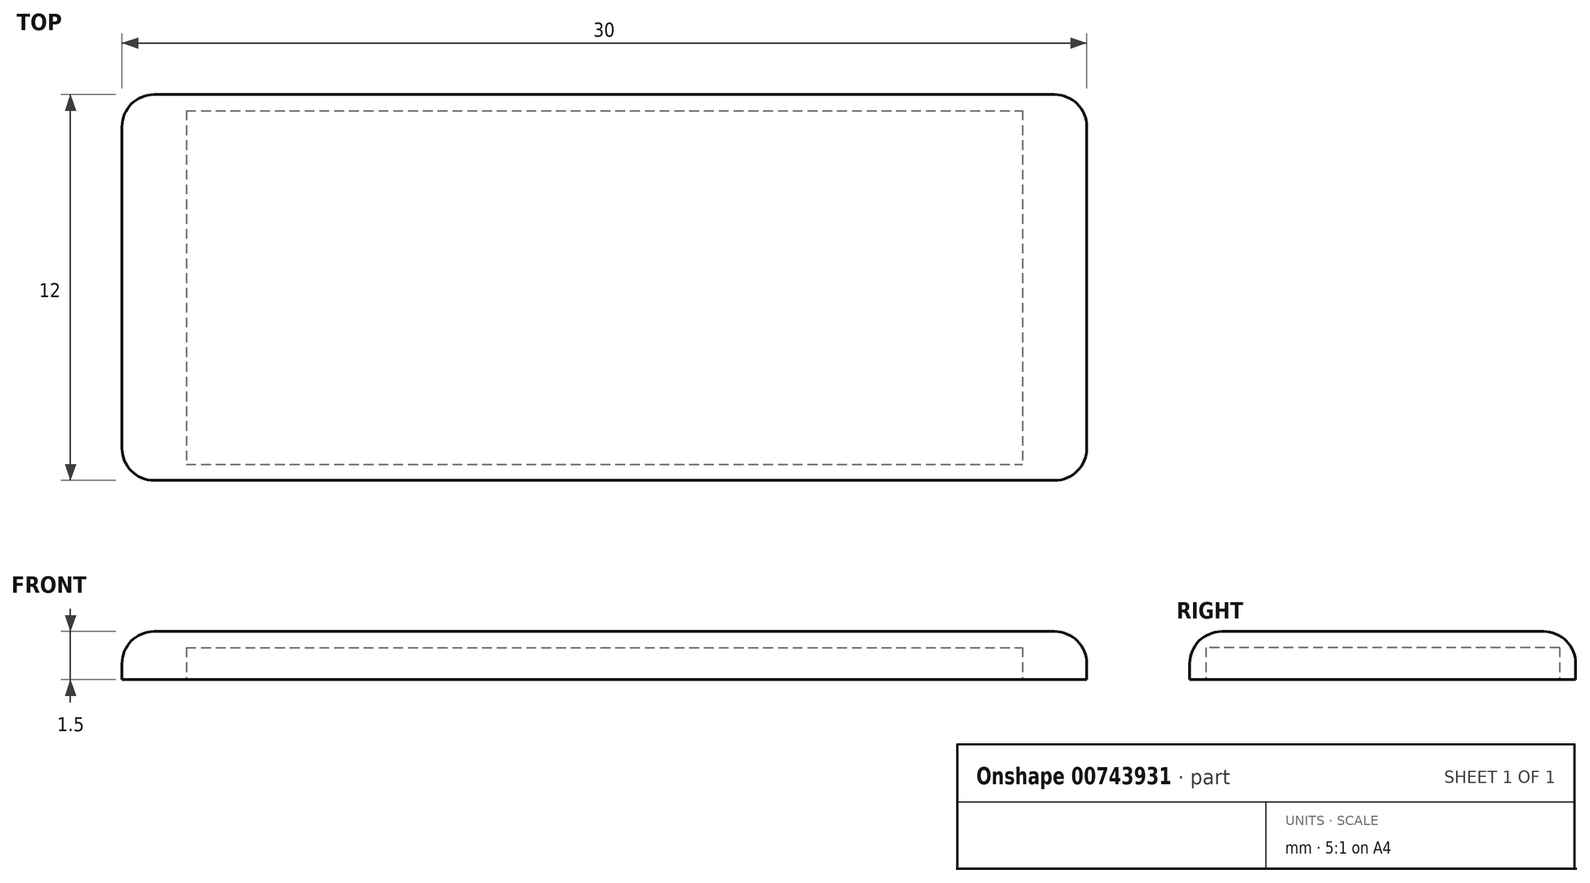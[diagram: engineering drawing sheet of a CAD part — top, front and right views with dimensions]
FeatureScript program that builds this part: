
annotation { "Feature Type Name" : "Feature", "Feature Type Description" : "" }
export const myFeature = defineFeature(function(context is Context, id is Id, definition is map)
    precondition{}
    {
        {
            var Q0;
            Q0=qCreatedBy(makeId("Top.planeOp"),FACE);
            var sketch = newSketch(context, id + "F0", { "sketchPlane" : qUnion([Q0])});
            skLineSegment(sketch, "E0.bottom", {"start": v(1, 0) * mm, "end": v(29, 0) * mm});
            skLineSegment(sketch, "E0.top", {"start": v(1, 12) * mm, "end": v(29, 12) * mm});
            skLineSegment(sketch, "E0.left", {"start": v(0, 1) * mm, "end": v(0, 11) * mm});
            skLineSegment(sketch, "E0.right", {"start": v(30, 1) * mm, "end": v(30, 11) * mm});
            skPoint(sketch, "E1.visualSharp", {"position": v(30, 12) * mm});
            skArc(sketch, "E1.filletArc", {"start": v(30, 11) * mm, "mid": v(29.7, 11.7) * mm, "end": v(29, 12) * mm});
            skPoint(sketch, "E2.visualSharp", {"position": v(30, 0) * mm});
            skArc(sketch, "E2.filletArc", {"start": v(29, 0) * mm, "mid": v(29.7, 0.3) * mm, "end": v(30, 1) * mm});
            skPoint(sketch, "E3.visualSharp", {"position": v(0, 0) * mm});
            skArc(sketch, "E3.filletArc", {"start": v(0, 1) * mm, "mid": v(0.3, 0.3) * mm, "end": v(1, 0) * mm});
            skPoint(sketch, "E4.visualSharp", {"position": v(0, 12) * mm});
            skArc(sketch, "E4.filletArc", {"start": v(1, 12) * mm, "mid": v(0.3, 11.7) * mm, "end": v(0, 11) * mm});
            skSolve(sketch);
        }
        {
            var Q0;
            Q0=makeQuery(id+"F0.imprint","IMPRINT",FACE,{"disambiguationData":[TD([[makeQuery(id+"F0.imprint","IMPRINT",EDGE,{"derivedFrom":sQuery(id+"F0.wireOp",EDGE,"E0.bottom")}),1.0]])]});
            extrude(context, id + "F1", {"entities" : qUnion([Q0]), "depth" : 1.5 * mm, "offsetDistance" : 25 * mm});
        }
        {
            var Q0;
            Q0=makeQuery(id+"F1.opExtrude","CAP_FACE",FACE,{"disambiguationData":[OSD([sQuery(id+"F0.wireOp",EDGE,"E0.bottom"),sQuery(id+"F0.wireOp",EDGE,"E0.top"),sQuery(id+"F0.wireOp",EDGE,"E0.left"),sQuery(id+"F0.wireOp",EDGE,"E0.right"),sQuery(id+"F0.wireOp",EDGE,"E1.filletArc"),sQuery(id+"F0.wireOp",EDGE,"E2.filletArc"),sQuery(id+"F0.wireOp",EDGE,"E3.filletArc"),sQuery(id+"F0.wireOp",EDGE,"E4.filletArc")])],"isStart":false});
            fillet(context, id + "F2", {"entities" : qUnion([Q0]), "radius" : 1 * mm, "tangentPropagation" : true, "allowEdgeOverflow" : false});
        }
        {
            var Q0;
            Q0=qCreatedBy(makeId("Top.planeOp"),FACE);
            var sketch = newSketch(context, id + "F3", { "sketchPlane" : qUnion([Q0])});
            skLineSegment(sketch, "E5.bottom", {"start": v(2, 11.5) * mm, "end": v(28, 11.5) * mm});
            skLineSegment(sketch, "E5.top", {"start": v(2, 0.5) * mm, "end": v(28, 0.5) * mm});
            skLineSegment(sketch, "E5.left", {"start": v(2, 11.5) * mm, "end": v(2, 0.5) * mm});
            skLineSegment(sketch, "E5.right", {"start": v(28, 11.5) * mm, "end": v(28, 0.5) * mm});
            skSolve(sketch);
        }
        {
            var Q0;
            Q0 = qSketchRegion(id + "F3", true);
            extrude(context, id + "F4", {"entities" : qUnion([Q0]), "operationType" : NewBodyOperationType.REMOVE, "depth" : 1 * mm, "offsetDistance" : 25 * mm});
        }
    });
